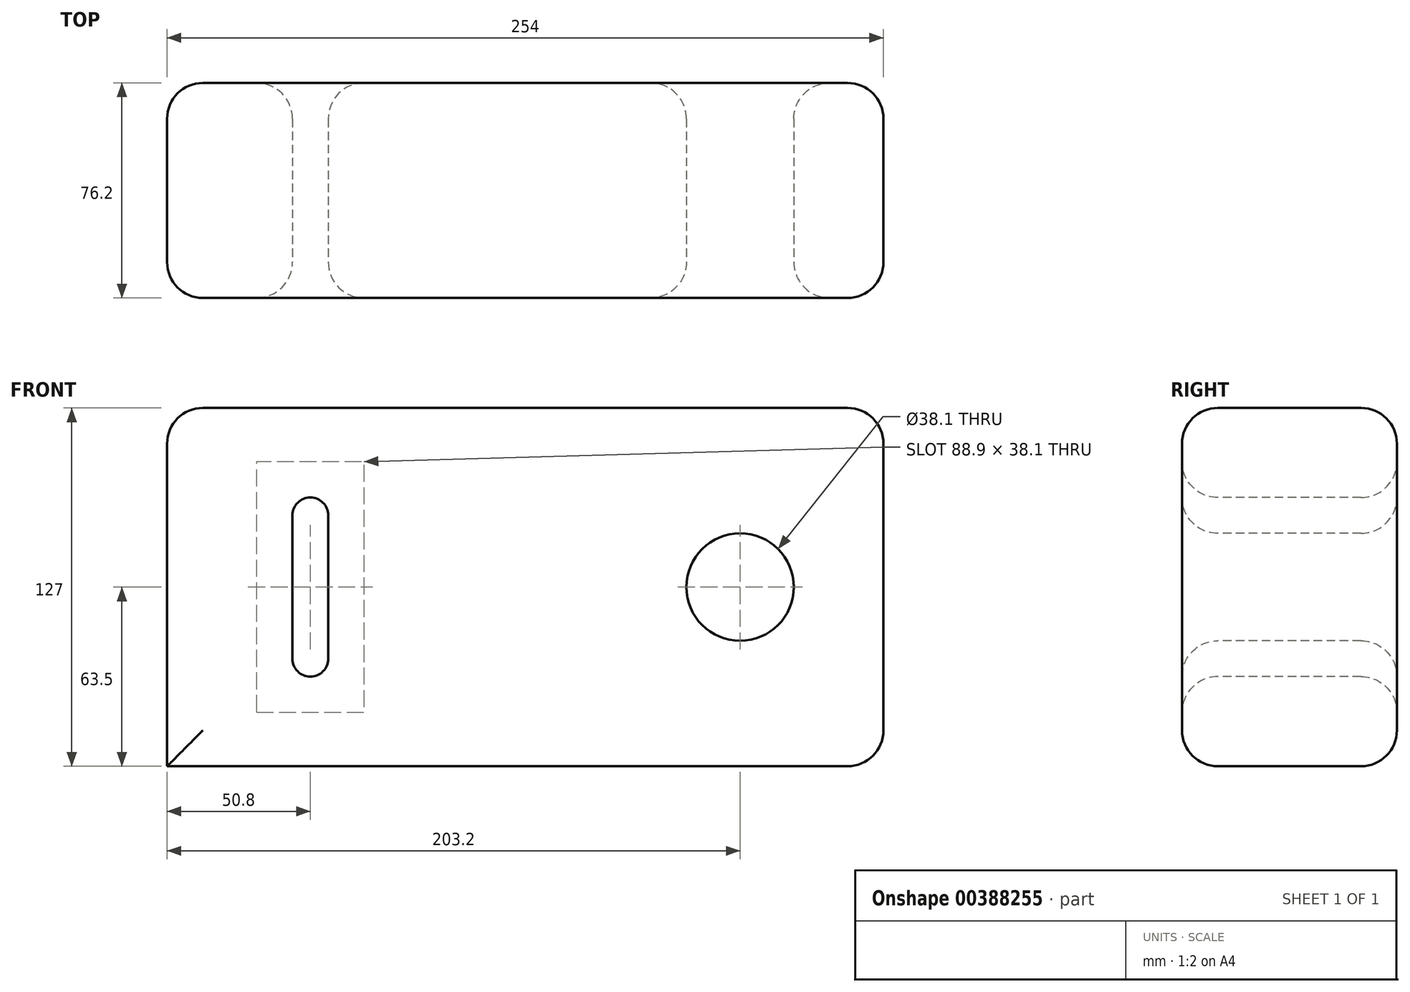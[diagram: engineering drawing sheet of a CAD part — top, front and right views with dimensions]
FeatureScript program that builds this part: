
annotation { "Feature Type Name" : "Feature", "Feature Type Description" : "" }
export const myFeature = defineFeature(function(context is Context, id is Id, definition is map)
    precondition{}
    {
        {
            var Q0;
            Q0=qCreatedBy(makeId("Front.planeOp"),FACE);
            var sketch = newSketch(context, id + "F0", { "sketchPlane" : qUnion([Q0])});
            skLineSegment(sketch, "E0.bottom", {"start": v(0, 0) * mm, "end": v(254, 0) * mm});
            skLineSegment(sketch, "E0.top", {"start": v(0, 127) * mm, "end": v(254, 127) * mm});
            skLineSegment(sketch, "E0.left", {"start": v(0, 0) * mm, "end": v(0, 127) * mm});
            skLineSegment(sketch, "E0.right", {"start": v(254, 0) * mm, "end": v(254, 127) * mm});
            skSolve(sketch);
        }
        {
            var Q0;
            Q0 = qSketchRegion(id + "F0", true);
            extrude(context, id + "F1", {"entities" : qUnion([Q0]), "depth" : 76.2 * mm});
        }
        {
            var Q0;
            Q0=makeQuery(id+"F1.opExtrude","CAP_FACE",FACE,{"disambiguationData":[OSD([sQuery(id+"F0.wireOp",EDGE,"E0.bottom"),sQuery(id+"F0.wireOp",EDGE,"E0.top"),sQuery(id+"F0.wireOp",EDGE,"E0.left"),sQuery(id+"F0.wireOp",EDGE,"E0.right")])],"isStart":false});
            var sketch = newSketch(context, id + "F2", { "sketchPlane" : qUnion([Q0])});
            skCircle(sketch, "E1", {"center": v(203.2, 63.5) * mm, "radius": 19.05 * mm});
            skSolve(sketch);
        }
        {
            var Q0;
            Q0=makeQuery(id+"F2.imprint","IMPRINT",FACE,{"disambiguationData":[TD([[makeQuery(id+"F2.imprint","IMPRINT",EDGE,{"derivedFrom":sQuery(id+"F2.wireOp",EDGE,"E1")}),1.0]])]});
            var Q1;
            Q1=sQuery(id+"F2.wireOp",EDGE,"E1");
            extrude(context, id + "F3", {"entities" : qUnion([Q0]), "operationType" : NewBodyOperationType.REMOVE, "surfaceEntities" : qUnion([Q1]), "endBound" : BoundingType.THROUGH_ALL, "oppositeDirection" : true, "depth" : 25.4 * mm});
        }
        {
            var Q0;
            Q0=makeQuery(id+"F1.opExtrude","CAP_FACE",FACE,{"disambiguationData":[OSD([sQuery(id+"F0.wireOp",EDGE,"E0.bottom"),sQuery(id+"F0.wireOp",EDGE,"E0.top"),sQuery(id+"F0.wireOp",EDGE,"E0.left"),sQuery(id+"F0.wireOp",EDGE,"E0.right")])],"isStart":false});
            var sketch = newSketch(context, id + "F4", { "sketchPlane" : qUnion([Q0])});
            skArc(sketch, "E2", {"start": v(57.15, 88.9) * mm, "mid": v(50.8, 95.25) * mm, "end": v(44.45, 88.9) * mm});
            skArc(sketch, "E3", {"start": v(44.45, 38.1) * mm, "mid": v(50.8, 31.75) * mm, "end": v(57.15, 38.1) * mm});
            skLineSegment(sketch, "E4", {"start": v(57.15, 88.9) * mm, "end": v(57.15, 38.1) * mm});
            skLineSegment(sketch, "E5", {"start": v(44.45, 38.1) * mm, "end": v(44.45, 88.9) * mm});
            skPoint(sketch, "E6", {"position": v(50.8, 63.5) * mm});
            skSolve(sketch);
        }
        {
            var Q0;
            Q0 = qSketchRegion(id + "F4", true);
            extrude(context, id + "F5", {"entities" : qUnion([Q0]), "operationType" : NewBodyOperationType.REMOVE, "endBound" : BoundingType.THROUGH_ALL, "oppositeDirection" : true, "depth" : 25.4 * mm});
        }
        {
            var Q0;
            Q0=makeQuery(id+"F1.opExtrude","CAP_FACE",FACE,{"disambiguationData":[OSD([sQuery(id+"F0.wireOp",EDGE,"E0.bottom"),sQuery(id+"F0.wireOp",EDGE,"E0.top"),sQuery(id+"F0.wireOp",EDGE,"E0.left"),sQuery(id+"F0.wireOp",EDGE,"E0.right")])],"isStart":false});
            fillet(context, id + "F6", {"entities" : qUnion([Q0]), "radius" : 12.7 * mm, "tangentPropagation" : true, "allowEdgeOverflow" : false});
        }
        {
            var Q0;
            Q0=makeQuery(id+"F1.opExtrude","CAP_EDGE",EDGE,{"disambiguationData":[OSD([sQuery(id+"F0.wireOp",EDGE,"E0.top")])],"isStart":true});
            var Q1;
            Q1=makeQuery(id+"F1.opExtrude","SWEPT_EDGE",EDGE,{"disambiguationData":[OSD([sQuery(id+"F0.wireOp",EDGE,"E0.top"),sQuery(id+"F0.wireOp",EDGE,"E0.left")])]});
            var Q2;
            Q2=makeQuery(id+"F1.opExtrude","SWEPT_EDGE",EDGE,{"disambiguationData":[OSD([sQuery(id+"F0.wireOp",EDGE,"E0.top"),sQuery(id+"F0.wireOp",EDGE,"E0.right")])]});
            var Q3;
            Q3=makeQuery(id+"F1.opExtrude","CAP_EDGE",EDGE,{"disambiguationData":[OSD([sQuery(id+"F0.wireOp",EDGE,"E0.right")])],"isStart":true});
            var Q4;
            Q4=makeQuery(id+"F1.opExtrude","SWEPT_EDGE",EDGE,{"disambiguationData":[OSD([sQuery(id+"F0.wireOp",EDGE,"E0.bottom"),sQuery(id+"F0.wireOp",EDGE,"E0.right")])]});
            var Q5;
            Q5=makeQuery(id+"F1.opExtrude","CAP_EDGE",EDGE,{"disambiguationData":[OSD([sQuery(id+"F0.wireOp",EDGE,"E0.bottom")])],"isStart":true});
            var Q6;
            Q6=makeQuery(id+"F1.opExtrude","CAP_EDGE",EDGE,{"disambiguationData":[OSD([sQuery(id+"F0.wireOp",EDGE,"E0.left")])],"isStart":true});
            var Q7;
            Q7=makeQuery(id+"F5.boolean.opBoolean","INTERSECT",EDGE,{"derivedFrom":[makeQuery(id+"F1.opExtrude","CAP_FACE",FACE,{"disambiguationData":[OSD([sQuery(id+"F0.wireOp",EDGE,"E0.bottom"),sQuery(id+"F0.wireOp",EDGE,"E0.top"),sQuery(id+"F0.wireOp",EDGE,"E0.left"),sQuery(id+"F0.wireOp",EDGE,"E0.right")])],"isStart":true}),makeQuery(id+"F5.opExtrude","SWEPT_FACE",FACE,{"disambiguationData":[OSD([sQuery(id+"F4.wireOp",EDGE,"E5")])]})]});
            var Q8;
            Q8=makeQuery(id+"F5.boolean.opBoolean","INTERSECT",EDGE,{"derivedFrom":[makeQuery(id+"F1.opExtrude","CAP_FACE",FACE,{"disambiguationData":[OSD([sQuery(id+"F0.wireOp",EDGE,"E0.bottom"),sQuery(id+"F0.wireOp",EDGE,"E0.top"),sQuery(id+"F0.wireOp",EDGE,"E0.left"),sQuery(id+"F0.wireOp",EDGE,"E0.right")])],"isStart":true}),makeQuery(id+"F5.opExtrude","SWEPT_FACE",FACE,{"disambiguationData":[OSD([sQuery(id+"F4.wireOp",EDGE,"E3")])]})]});
            var Q9;
            Q9=makeQuery(id+"F5.boolean.opBoolean","INTERSECT",EDGE,{"derivedFrom":[makeQuery(id+"F1.opExtrude","CAP_FACE",FACE,{"disambiguationData":[OSD([sQuery(id+"F0.wireOp",EDGE,"E0.bottom"),sQuery(id+"F0.wireOp",EDGE,"E0.top"),sQuery(id+"F0.wireOp",EDGE,"E0.left"),sQuery(id+"F0.wireOp",EDGE,"E0.right")])],"isStart":true}),makeQuery(id+"F5.opExtrude","SWEPT_FACE",FACE,{"disambiguationData":[OSD([sQuery(id+"F4.wireOp",EDGE,"E4")])]})]});
            var Q10;
            Q10=makeQuery(id+"F5.boolean.opBoolean","INTERSECT",EDGE,{"derivedFrom":[makeQuery(id+"F1.opExtrude","CAP_FACE",FACE,{"disambiguationData":[OSD([sQuery(id+"F0.wireOp",EDGE,"E0.bottom"),sQuery(id+"F0.wireOp",EDGE,"E0.top"),sQuery(id+"F0.wireOp",EDGE,"E0.left"),sQuery(id+"F0.wireOp",EDGE,"E0.right")])],"isStart":true}),makeQuery(id+"F5.opExtrude","SWEPT_FACE",FACE,{"disambiguationData":[OSD([sQuery(id+"F4.wireOp",EDGE,"E2")])]})]});
            var Q11;
            Q11=makeQuery(id+"F3.boolean.opBoolean","INTERSECT",EDGE,{"derivedFrom":[makeQuery(id+"F1.opExtrude","CAP_FACE",FACE,{"disambiguationData":[OSD([sQuery(id+"F0.wireOp",EDGE,"E0.bottom"),sQuery(id+"F0.wireOp",EDGE,"E0.top"),sQuery(id+"F0.wireOp",EDGE,"E0.left"),sQuery(id+"F0.wireOp",EDGE,"E0.right")])],"isStart":true}),makeQuery(id+"F3.opExtrude","SWEPT_FACE",FACE,{"disambiguationData":[OSD([sQuery(id+"F2.wireOp",EDGE,"E1")])]})]});
            fillet(context, id + "F7", {"entities" : qUnion([Q0, Q1, Q2, Q3, Q4, Q5, Q6, Q7, Q8, Q9, Q10, Q11]), "radius" : 12.7 * mm, "tangentPropagation" : true, "allowEdgeOverflow" : false});
        }
        {
            var Q0;
            Q0=qCreatedBy(makeId("Top.planeOp"),FACE);
            cPlane(context, id + "F8", {"entities" : qUnion([Q0]), "cplaneType" : CPlaneType.OFFSET, "offset" : 63.5 * mm, "width" : 152.4 * mm, "height" : 152.4 * mm});
        }
    });
